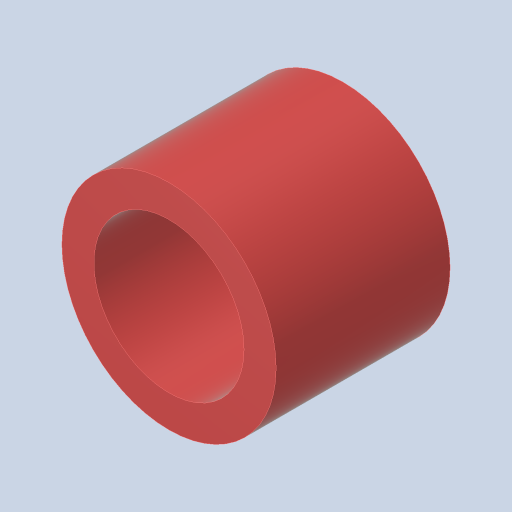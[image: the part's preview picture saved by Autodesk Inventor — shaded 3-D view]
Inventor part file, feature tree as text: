
AUTODESK INVENTOR PART (.ipt)
format: ipt  version: 2023.4 (Build 274418000, 418)  size: 117,760 bytes
history: native  units: in
note: dims shown in document units (in); Inventor stores cm internally (conversion verified against a paired STEP export)
features: extrude x1, sketch x1
ambient origin geometry x8: Origin, YZ Plane, XZ Plane, XY Plane, X Axis, Y Axis, Z Axis, Center Point
bodies: Solid1 (feature_tree)
feature tree (2):
  extrude  "Extrusion1"  Depth=0.678in
  sketch  "Sketch1"  dims[d0=0.585in d1=0.125in d2=0.678in d3=0.0in]
